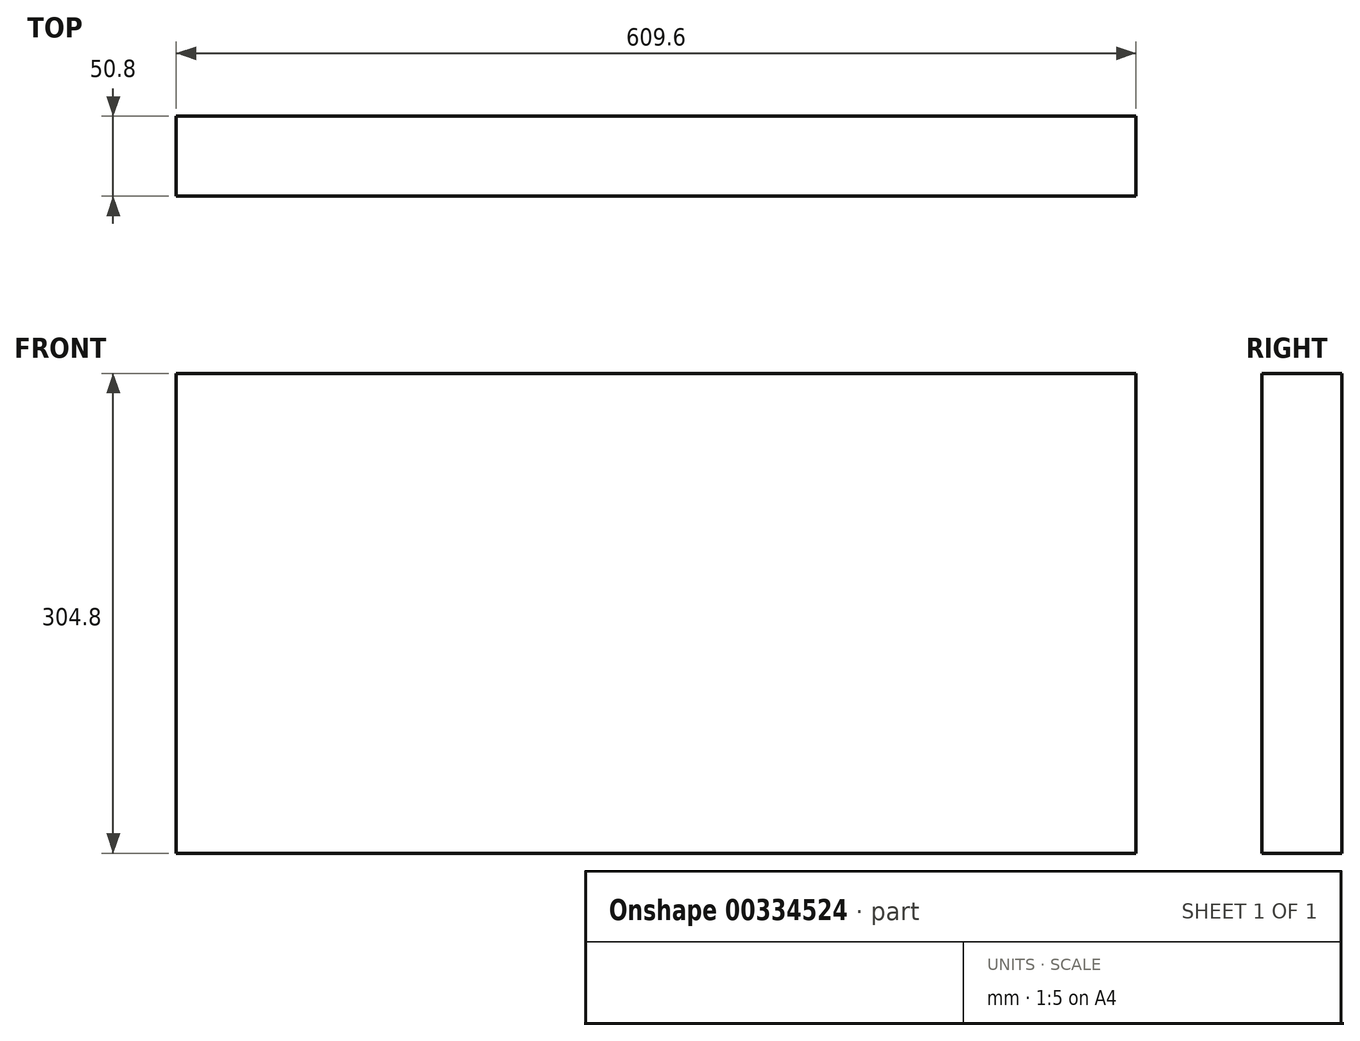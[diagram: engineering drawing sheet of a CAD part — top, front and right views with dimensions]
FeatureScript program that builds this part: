
annotation { "Feature Type Name" : "Feature", "Feature Type Description" : "" }
export const myFeature = defineFeature(function(context is Context, id is Id, definition is map)
    precondition{}
    {
        {
            var Q0;
            Q0=qCreatedBy(makeId("Front.planeOp"),FACE);
            var sketch = newSketch(context, id + "F0", { "sketchPlane" : qUnion([Q0])});
            skLineSegment(sketch, "E0.bottom", {"start": v(-151.85, 118.33) * mm, "end": v(457.75, 118.33) * mm});
            skLineSegment(sketch, "E0.top", {"start": v(-151.85, -186.47) * mm, "end": v(457.75, -186.47) * mm});
            skLineSegment(sketch, "E0.left", {"start": v(-151.85, 118.33) * mm, "end": v(-151.85, -186.47) * mm});
            skLineSegment(sketch, "E0.right", {"start": v(457.75, 118.33) * mm, "end": v(457.75, -186.47) * mm});
            skSolve(sketch);
        }
        {
            var Q0;
            Q0=makeQuery(id+"F0.imprint","IMPRINT",FACE,{"disambiguationData":[TD([[makeQuery(id+"F0.imprint","IMPRINT",EDGE,{"derivedFrom":sQuery(id+"F0.wireOp",EDGE,"E0.bottom")}),-1.0]])]});
            extrude(context, id + "F1", {"entities" : qUnion([Q0]), "depth" : 50.8 * mm});
        }
    });
